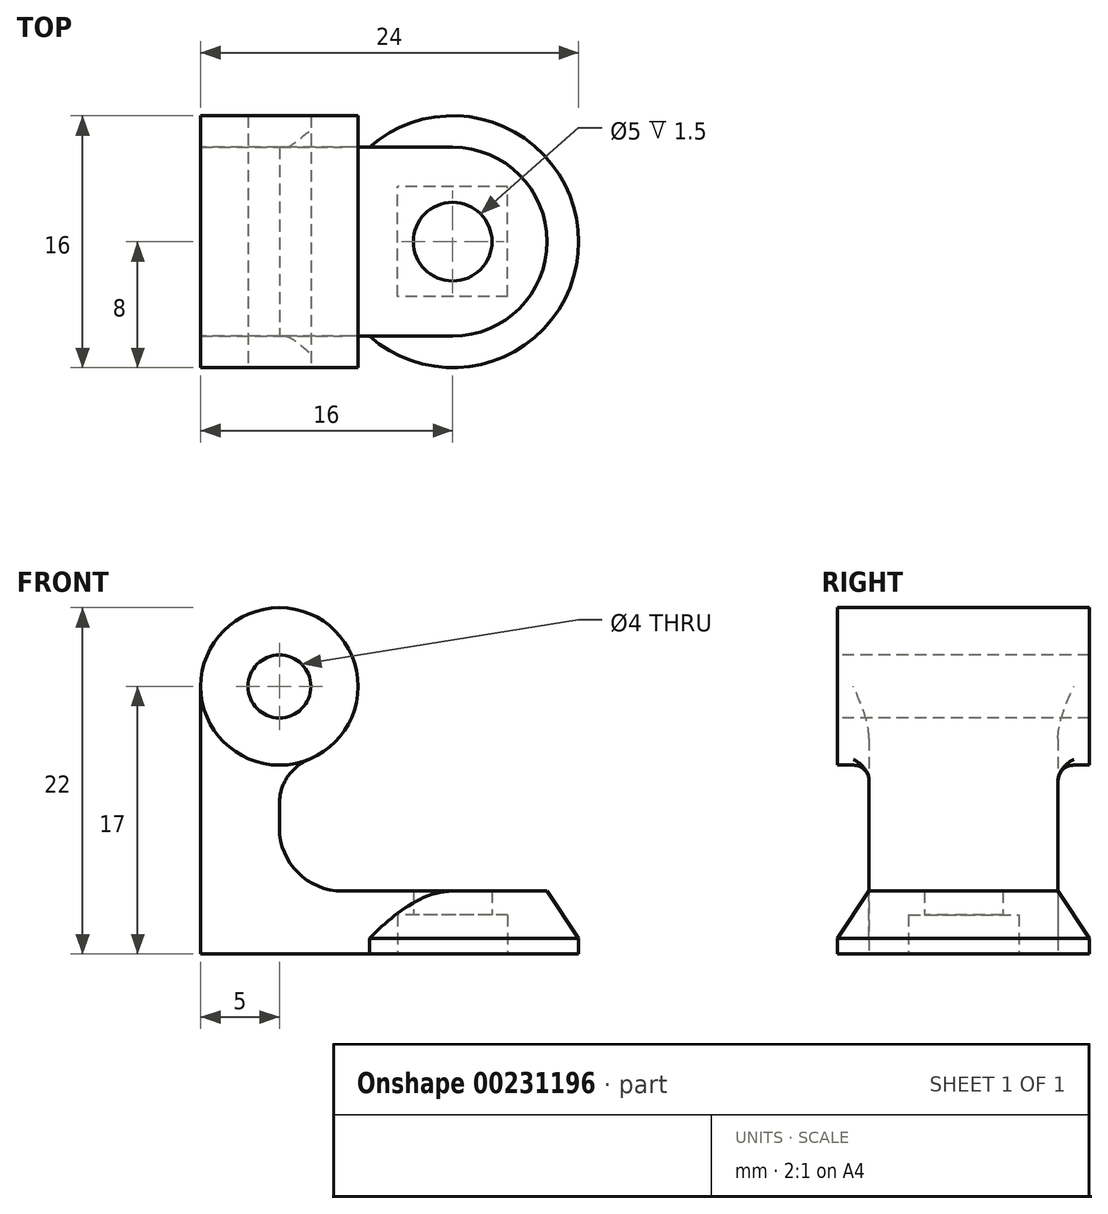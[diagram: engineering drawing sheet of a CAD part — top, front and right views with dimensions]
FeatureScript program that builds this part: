
annotation { "Feature Type Name" : "Feature", "Feature Type Description" : "" }
export const myFeature = defineFeature(function(context is Context, id is Id, definition is map)
    precondition{}
    {
        {
            var Q0;
            Q0=qCreatedBy(makeId("Top.planeOp"),FACE);
            var sketch = newSketch(context, id + "F0", { "sketchPlane" : qUnion([Q0])});
            skLineSegment(sketch, "E0.bottom", {"start": v(12, 6) * mm, "end": v(-12, 6) * mm});
            skLineSegment(sketch, "E0.top", {"start": v(12, -6) * mm, "end": v(-12, -6) * mm});
            skLineSegment(sketch, "E0.left", {"start": v(12, 6) * mm, "end": v(12, -6) * mm});
            skLineSegment(sketch, "E0.right", {"start": v(-12, 6) * mm, "end": v(-12, -6) * mm});
            skPoint(sketch, "E0.middle", {"position": v(0, 0) * mm});
            skCircle(sketch, "E1", {"center": v(4, 0) * mm, "radius": 8 * mm});
            skCircle(sketch, "E2", {"center": v(4, 0) * mm, "radius": 2.5 * mm});
            skLineSegment(sketch, "E3.bottom", {"start": v(7.5, 3.5) * mm, "end": v(0.5, 3.5) * mm});
            skLineSegment(sketch, "E3.top", {"start": v(7.5, -3.5) * mm, "end": v(0.5, -3.5) * mm});
            skLineSegment(sketch, "E3.left", {"start": v(7.5, -3.5) * mm, "end": v(7.5, 3.5) * mm});
            skLineSegment(sketch, "E3.right", {"start": v(0.5, -3.5) * mm, "end": v(0.5, 3.5) * mm});
            skLineSegment(sketch, "E4", {"start": v(-7, -6) * mm, "end": v(-7, 6) * mm});
            skSolve(sketch);
        }
        {
            var Q0;
            {var subQ0=sQuery(id+"F0.wireOp",EDGE,"E0.right");Q0=makeQuery(id+"F0.imprint","IMPRINT",FACE,{"disambiguationData":[TD([[makeQuery(id+"F0.imprint","IMPRINT",EDGE,{"derivedFrom":subQ0}),1.0]])]});}
            var Q1;
            Q1=makeQuery(id+"F0.imprint","IMPRINT",FACE,{"disambiguationData":[TD([[makeQuery(id+"F0.imprint","IMPRINT",EDGE,{"derivedFrom":sQuery(id+"F0.wireOp",EDGE,"E3.bottom")}),-1.0]])]});
            var Q2;
            {var subQ0=sQuery(id+"F0.wireOp",EDGE,"E1");var subQ1=sQuery(id+"F0.wireOp",EDGE,"E0.top");var subQ2=makeQuery(id+"F0.imprint","INTERSECT",VERTEX,{"disambiguationData":[OD(0.0)],"derivedFrom":[subQ1,subQ0]});Q2=makeQuery(id+"F0.imprint","IMPRINT",FACE,{"disambiguationData":[TD([[makeQuery(id+"F0.imprint","IMPRINT",EDGE,{"disambiguationData":[TD([[subQ2,-1.0]])],"derivedFrom":subQ1}),1.0]])]});}
            var Q3;
            {var subQ0=sQuery(id+"F0.wireOp",EDGE,"E1");var subQ1=sQuery(id+"F0.wireOp",EDGE,"E0.bottom");var subQ2=makeQuery(id+"F0.imprint","INTERSECT",VERTEX,{"disambiguationData":[OD(0.0)],"derivedFrom":[subQ1,subQ0]});Q3=makeQuery(id+"F0.imprint","IMPRINT",FACE,{"disambiguationData":[TD([[makeQuery(id+"F0.imprint","IMPRINT",EDGE,{"disambiguationData":[TD([[subQ2,-1.0]])],"derivedFrom":subQ1}),-1.0]])]});}
            extrude(context, id + "F1", {"entities" : qUnion([Q0, Q1, Q2, Q3]), "depth" : 4 * mm});
        }
        {
            var Q0;
            Q0=makeQuery(id+"F0.imprint","IMPRINT",FACE,{"disambiguationData":[TD([[makeQuery(id+"F0.imprint","IMPRINT",EDGE,{"derivedFrom":sQuery(id+"F0.wireOp",EDGE,"E2")}),-1.0]])]});
            extrude(context, id + "F2", {"entities" : qUnion([Q0]), "operationType" : NewBodyOperationType.ADD, "depth" : 4 * mm, "hasSecondDirection" : true, "secondDirectionOppositeDirection" : false, "secondDirectionDepth" : 2.5 * mm});
        }
        {
            var Q0;
            Q0=makeQuery(id+"F1.opExtrude","SWEPT_BODY",BODY,{"disambiguationData":[OSD([sQuery(id+"F0.wireOp",EDGE,"E0.bottom"),sQuery(id+"F0.wireOp",EDGE,"E0.top"),sQuery(id+"F0.wireOp",EDGE,"E0.right"),sQuery(id+"F0.wireOp",EDGE,"E4")])]});
            deleteBodies(context, id + "F3", {"entities" : qUnion([Q0])});
        }
        {
            var Q0;
            {var subQ0=sQuery(id+"F0.wireOp",EDGE,"E0.right");Q0=makeQuery(id+"F0.imprint","IMPRINT",FACE,{"disambiguationData":[TD([[makeQuery(id+"F0.imprint","IMPRINT",EDGE,{"derivedFrom":subQ0}),1.0]])]});}
            var Q1;
            {var subQ0=sQuery(id+"F0.wireOp",EDGE,"E4");Q1=makeQuery(id+"F0.imprint","IMPRINT",FACE,{"disambiguationData":[TD([[makeQuery(id+"F0.imprint","IMPRINT",EDGE,{"derivedFrom":subQ0}),-1.0]])]});}
            extrude(context, id + "F4", {"entities" : qUnion([Q0, Q1]), "operationType" : NewBodyOperationType.ADD, "depth" : 4 * mm});
        }
        {
            var Q0;
            {var subQ0=sQuery(id+"F0.wireOp",EDGE,"E0.right");Q0=makeQuery(id+"F0.imprint","IMPRINT",FACE,{"disambiguationData":[TD([[makeQuery(id+"F0.imprint","IMPRINT",EDGE,{"derivedFrom":subQ0}),1.0]])]});}
            extrude(context, id + "F5", {"entities" : qUnion([Q0]), "operationType" : NewBodyOperationType.ADD, "depth" : 17 * mm});
        }
        {
            var Q0;
            Q0=makeQuery(id+"F1.opExtrude","CAP_EDGE",EDGE,{"disambiguationData":[OSD([sQuery(id+"F0.wireOp",EDGE,"E1")])],"isStart":false});
            chamfer(context, id + "F6", {"entities" : qUnion([Q0]), "chamferType" : ChamferType.TWO_OFFSETS, "width1" : 2 * mm, "oppositeDirection" : false, "width2" : 3 * mm, "tangentPropagation" : true});
        }
        {
            var Q0;
            Q0=qCreatedBy(makeId("Front.planeOp"),FACE);
            var sketch = newSketch(context, id + "F7", { "sketchPlane" : qUnion([Q0])});
            skCircle(sketch, "E5", {"center": v(-7, 17) * mm, "radius": 5 * mm});
            skCircle(sketch, "E6", {"center": v(-7, 17) * mm, "radius": 2 * mm});
            skSolve(sketch);
        }
        {
            var Q0;
            Q0=makeQuery(id+"F7.imprint","IMPRINT",FACE,{"disambiguationData":[TD([[makeQuery(id+"F7.imprint","IMPRINT",EDGE,{"derivedFrom":sQuery(id+"F7.wireOp",EDGE,"E6")}),1.0]])]});
            extrude(context, id + "F8", {"entities" : qUnion([Q0]), "operationType" : NewBodyOperationType.REMOVE, "oppositeDirection" : true, "depth" : 25 * mm, "hasSecondDirection" : true, "secondDirectionOppositeDirection" : false, "secondDirectionDepth" : 25 * mm});
        }
        {
            var Q0;
            {var subQ0=sQuery(id+"F0.wireOp",EDGE,"E1");var subQ1=sQuery(id+"F0.wireOp",EDGE,"E3.right");var subQ2=sQuery(id+"F0.wireOp",EDGE,"E3.left");var subQ3=sQuery(id+"F0.wireOp",EDGE,"E3.top");var subQ4=sQuery(id+"F0.wireOp",EDGE,"E3.bottom");Q0=makeQuery(id+"F5.boolean.opBoolean","INTERSECT",EDGE,{"derivedFrom":[makeQuery(id+"F4.boolean.opBoolean","MERGE",FACE,{"derivedFrom":[makeQuery(id+"F2.boolean.opBoolean","MERGE",FACE,{"derivedFrom":[makeQuery(id+"F1.opExtrude","CAP_FACE",FACE,{"disambiguationData":[OSD([subQ0,subQ4,subQ3,subQ2,subQ1])],"isStart":false}),makeQuery(id+"F2.opExtrude","CAP_FACE",FACE,{"disambiguationData":[OSD([sQuery(id+"F0.wireOp",EDGE,"E2"),subQ4,subQ3,subQ2,subQ1])],"isStart":false})]}),makeQuery(id+"F4.opExtrude","CAP_FACE",FACE,{"disambiguationData":[OSD([sQuery(id+"F0.wireOp",EDGE,"E0.bottom"),sQuery(id+"F0.wireOp",EDGE,"E0.top"),sQuery(id+"F0.wireOp",EDGE,"E0.right"),subQ0])],"isStart":false})]}),makeQuery(id+"F5.opExtrude","SWEPT_FACE",FACE,{"disambiguationData":[OSD([sQuery(id+"F0.wireOp",EDGE,"E4")])]})]});}
            fillet(context, id + "F9", {"entities" : qUnion([Q0]), "tangentPropagation" : true, "radius" : 4 * mm, "defaultsChanged" : true, "vertexSettings" : [], "allowEdgeOverflow" : false});
        }
        {
            var Q0;
            Q0 = qSketchRegion(id + "F7", true);
            extrude(context, id + "F10", {"entities" : qUnion([Q0]), "operationType" : NewBodyOperationType.ADD, "endBound" : BoundingType.SYMMETRIC, "depth" : 16 * mm, "offsetDistance" : 25 * mm});
        }
        {
            var Q0;
            Q0=makeQuery(id+"F10.boolean.opBoolean","INTERSECT",EDGE,{"derivedFrom":[makeQuery(id+"F5.opExtrude","SWEPT_FACE",FACE,{"disambiguationData":[OSD([sQuery(id+"F0.wireOp",EDGE,"E4")])]}),makeQuery(id+"F10.opExtrude","SWEPT_FACE",FACE,{"disambiguationData":[OSD([sQuery(id+"F7.wireOp",EDGE,"E5")])]})]});
            fillet(context, id + "F11", {"entities" : qUnion([Q0]), "tangentPropagation" : true, "radius" : 3 * mm, "defaultsChanged" : true, "vertexSettings" : [], "allowEdgeOverflow" : false});
        }
        {
            var Q0;
            {var subQ0=sQuery(id+"F0.wireOp",EDGE,"E0.top");Q0=makeQuery(id+"F10.boolean.opBoolean","INTERSECT",EDGE,{"derivedFrom":[makeQuery(id+"F5.boolean.opBoolean","MERGE",FACE,{"derivedFrom":[makeQuery(id+"F4.opExtrude","SWEPT_FACE",FACE,{"disambiguationData":[OSD([subQ0])]}),makeQuery(id+"F5.opExtrude","SWEPT_FACE",FACE,{"disambiguationData":[OSD([subQ0])]})]}),makeQuery(id+"F10.opExtrude","SWEPT_FACE",FACE,{"disambiguationData":[OSD([sQuery(id+"F7.wireOp",EDGE,"E5")])]})]});}
            var Q1;
            {var subQ0=sQuery(id+"F0.wireOp",EDGE,"E0.bottom");Q1=makeQuery(id+"F10.boolean.opBoolean","INTERSECT",EDGE,{"derivedFrom":[makeQuery(id+"F5.boolean.opBoolean","MERGE",FACE,{"derivedFrom":[makeQuery(id+"F4.opExtrude","SWEPT_FACE",FACE,{"disambiguationData":[OSD([subQ0])]}),makeQuery(id+"F5.opExtrude","SWEPT_FACE",FACE,{"disambiguationData":[OSD([subQ0])]})]}),makeQuery(id+"F10.opExtrude","SWEPT_FACE",FACE,{"disambiguationData":[OSD([sQuery(id+"F7.wireOp",EDGE,"E5")])]})]});}
            fillet(context, id + "F12", {"entities" : qUnion([Q0, Q1]), "tangentPropagation" : true, "radius" : 1 * mm, "defaultsChanged" : false, "vertexSettings" : [], "allowEdgeOverflow" : false});
        }
    });
